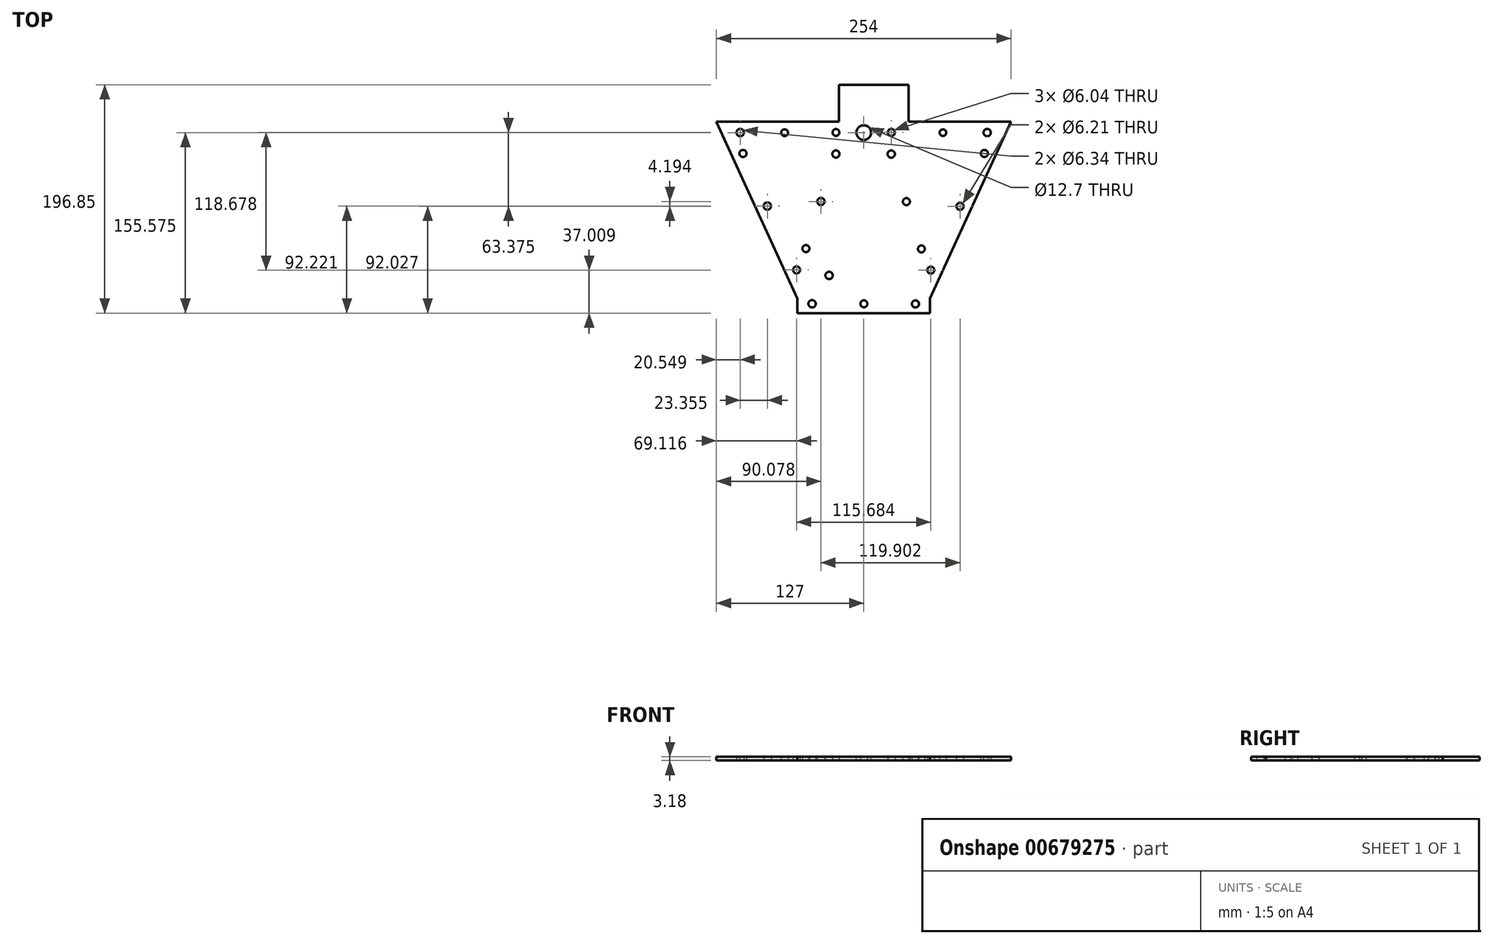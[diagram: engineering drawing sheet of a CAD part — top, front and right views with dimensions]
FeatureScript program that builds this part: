
annotation { "Feature Type Name" : "Feature", "Feature Type Description" : "" }
export const myFeature = defineFeature(function(context is Context, id is Id, definition is map)
    precondition{}
    {
        {
            var Q0;
            Q0=qCreatedBy(makeId("Top.planeOp"),FACE);
            var sketch = newSketch(context, id + "F0", { "sketchPlane" : qUnion([Q0])});
            skLineSegment(sketch, "E0.bottom", {"start": v(101.6, 76.2) * mm, "end": v(-152.4, 76.2) * mm});
            skLineSegment(sketch, "E0.top", {"start": v(31.75, -76.2) * mm, "end": v(-82.55, -76.2) * mm});
            skPoint(sketch, "E0.middle", {"position": v(0, 0) * mm});
            skLineSegment(sketch, "E1", {"start": v(-152.4, 76.2) * mm, "end": v(-82.55, -76.2) * mm});
            skLineSegment(sketch, "E2", {"start": v(101.6, 76.2) * mm, "end": v(31.75, -76.2) * mm});
            skPoint(sketch, "E3.orphan", {"position": v(-101.6, -76.2) * mm});
            skPoint(sketch, "E4.orphan", {"position": v(152.4, -76.2) * mm});
            skLineSegment(sketch, "E5.bottom", {"start": v(-82.55, -76.2) * mm, "end": v(31.75, -76.2) * mm});
            skLineSegment(sketch, "E5.top", {"start": v(-82.55, -88.9) * mm, "end": v(31.75, -88.9) * mm});
            skLineSegment(sketch, "E5.left", {"start": v(-82.55, -76.2) * mm, "end": v(-82.55, -88.9) * mm});
            skLineSegment(sketch, "E5.right", {"start": v(31.75, -76.2) * mm, "end": v(31.75, -88.9) * mm});
            skSolve(sketch);
        }
        {
            var Q0;
            Q0=qSketchRegion(id+"F0",true);
            extrude(context, id + "F1", {"entities" : qUnion([Q0]), "depth" : 3.17 * mm});
        }
        {
            var Q0;
            Q0=makeQuery(id+"F1.opExtrude","CAP_FACE",FACE,{"disambiguationData":[OSD([sQuery(id+"F0.wireOp",EDGE,"E0.bottom"),sQuery(id+"F0.wireOp",EDGE,"E0.top"),sQuery(id+"F0.wireOp",EDGE,"E1"),sQuery(id+"F0.wireOp",EDGE,"E2")])],"isStart":false});
            var sketch = newSketch(context, id + "F2", { "sketchPlane" : qUnion([Q0])});
            skCircle(sketch, "E6", {"center": v(-25.4, 66.67) * mm, "radius": 6.35 * mm});
            skSolve(sketch);
        }
        {
            var Q0;
            Q0=qSketchRegion(id+"F2",true);
            extrude(context, id + "F3", {"entities" : qUnion([Q0]), "operationType" : NewBodyOperationType.REMOVE, "oppositeDirection" : true, "depth" : 25.4 * mm});
        }
        {
            var Q0;
            Q0=makeQuery(id+"F1.opExtrude","CAP_FACE",FACE,{"disambiguationData":[OSD([sQuery(id+"F0.wireOp",EDGE,"E0.bottom"),sQuery(id+"F0.wireOp",EDGE,"E1"),sQuery(id+"F0.wireOp",EDGE,"E2"),sQuery(id+"F0.wireOp",EDGE,"E5.top"),sQuery(id+"F0.wireOp",EDGE,"E5.left"),sQuery(id+"F0.wireOp",EDGE,"E5.right")])],"isStart":true});
            var sketch = newSketch(context, id + "F4", { "sketchPlane" : qUnion([Q0])});
            skCircle(sketch, "E7", {"center": v(-83.28, 51.7) * mm, "radius": 3.02 * mm});
            skCircle(sketch, "E8", {"center": v(-75.22, 33.3) * mm, "radius": 3.03 * mm});
            skCircle(sketch, "E9", {"center": v(-108.5, -3.32) * mm, "radius": 3.17 * mm});
            skCircle(sketch, "E10", {"center": v(-129.5, -48.7) * mm, "radius": 3.07 * mm});
            skCircle(sketch, "E11", {"center": v(-131.85, -66.7) * mm, "radius": 3.17 * mm});
            skCircle(sketch, "E12", {"center": v(-93.6, -66.64) * mm, "radius": 2.93 * mm});
            skCircle(sketch, "E13", {"center": v(-49.32, -66.76) * mm, "radius": 2.95 * mm});
            skCircle(sketch, "E14", {"center": v(-49.38, -48.2) * mm, "radius": 3.1 * mm});
            skCircle(sketch, "E15", {"center": v(-62.32, -7.32) * mm, "radius": 3.1 * mm});
            skCircle(sketch, "E16", {"center": v(-1.62, -66.79) * mm, "radius": 3.02 * mm});
            skCircle(sketch, "E17", {"center": v(42.87, -66.63) * mm, "radius": 2.83 * mm});
            skCircle(sketch, "E18", {"center": v(80.98, -66.7) * mm, "radius": 3.16 * mm});
            skCircle(sketch, "E19", {"center": v(78.6, -48.7) * mm, "radius": 3.04 * mm});
            skCircle(sketch, "E20", {"center": v(-1.71, -48.15) * mm, "radius": 3.14 * mm});
            skCircle(sketch, "E21", {"center": v(11.36, -7.19) * mm, "radius": 3.04 * mm});
            skCircle(sketch, "E22", {"center": v(57.58, -3.13) * mm, "radius": 3.1 * mm});
            skCircle(sketch, "E23", {"center": v(24.3, 33.59) * mm, "radius": 3 * mm});
            skCircle(sketch, "E24", {"center": v(32.4, 51.9) * mm, "radius": 3.02 * mm});
            skSolve(sketch);
        }
        {
            var Q0;
            Q0=qSketchRegion(id+"F4",true);
            extrude(context, id + "F5", {"entities" : qUnion([Q0]), "operationType" : NewBodyOperationType.REMOVE, "oppositeDirection" : true, "depth" : 25.4 * mm, "offsetDistance" : 25.4 * mm});
        }
        {
            var Q0;
            Q0=makeQuery(id+"F1.opExtrude","CAP_FACE",FACE,{"disambiguationData":[OSD([sQuery(id+"F0.wireOp",EDGE,"E0.bottom"),sQuery(id+"F0.wireOp",EDGE,"E1"),sQuery(id+"F0.wireOp",EDGE,"E2"),sQuery(id+"F0.wireOp",EDGE,"E5.top"),sQuery(id+"F0.wireOp",EDGE,"E5.left"),sQuery(id+"F0.wireOp",EDGE,"E5.right")])],"isStart":true});
            var sketch = newSketch(context, id + "F6", { "sketchPlane" : qUnion([Q0])});
            skCircle(sketch, "E25", {"center": v(-69.92, 80.9) * mm, "radius": 3.19 * mm});
            skCircle(sketch, "E26", {"center": v(-25.26, 80.9) * mm, "radius": 2.98 * mm});
            skCircle(sketch, "E27", {"center": v(19.16, 81.01) * mm, "radius": 3.06 * mm});
            skSolve(sketch);
        }
        {
            var Q0;
            Q0=qSketchRegion(id+"F6",true);
            extrude(context, id + "F7", {"entities" : qUnion([Q0]), "operationType" : NewBodyOperationType.REMOVE, "oppositeDirection" : true, "depth" : 25.4 * mm, "offsetDistance" : 25.4 * mm});
        }
        {
            var Q0;
            Q0=makeQuery(id+"F1.opExtrude","CAP_FACE",FACE,{"disambiguationData":[OSD([sQuery(id+"F0.wireOp",EDGE,"E0.bottom"),sQuery(id+"F0.wireOp",EDGE,"E1"),sQuery(id+"F0.wireOp",EDGE,"E2"),sQuery(id+"F0.wireOp",EDGE,"E5.top"),sQuery(id+"F0.wireOp",EDGE,"E5.left"),sQuery(id+"F0.wireOp",EDGE,"E5.right")])],"isStart":true});
            var sketch = newSketch(context, id + "F8", { "sketchPlane" : qUnion([Q0])});
            skCircle(sketch, "E28", {"center": v(-55.24, 56.45) * mm, "radius": 3.18 * mm});
            skSolve(sketch);
        }
        {
            var Q0;
            Q0=qSketchRegion(id+"F8",true);
            extrude(context, id + "F9", {"entities" : qUnion([Q0]), "operationType" : NewBodyOperationType.REMOVE, "oppositeDirection" : true, "depth" : 25.4 * mm, "offsetDistance" : 25.4 * mm});
        }
        {
            var Q0;
            Q0=makeQuery(id+"F1.opExtrude","SWEPT_FACE",FACE,{"disambiguationData":[OSD([sQuery(id+"F0.wireOp",EDGE,"E0.bottom")])]});
            var sketch = newSketch(context, id + "F10", { "sketchPlane" : qUnion([Q0])});
            skLineSegment(sketch, "E29.bottom", {"start": v(-13.3, 3.18) * mm, "end": v(46.75, 3.18) * mm});
            skLineSegment(sketch, "E29.top", {"start": v(-13.3, 0) * mm, "end": v(46.75, 0) * mm});
            skLineSegment(sketch, "E29.left", {"start": v(-13.3, 3.18) * mm, "end": v(-13.3, 0) * mm});
            skLineSegment(sketch, "E29.right", {"start": v(46.75, 3.18) * mm, "end": v(46.75, 0) * mm});
            skSolve(sketch);
        }
        {
            var Q0;
            Q0 = qSketchRegion(id + "F10", true);
            extrude(context, id + "F11", {"entities" : qUnion([Q0]), "operationType" : NewBodyOperationType.ADD, "depth" : 31.75 * mm, "offsetDistance" : 25.4 * mm});
        }
    });
